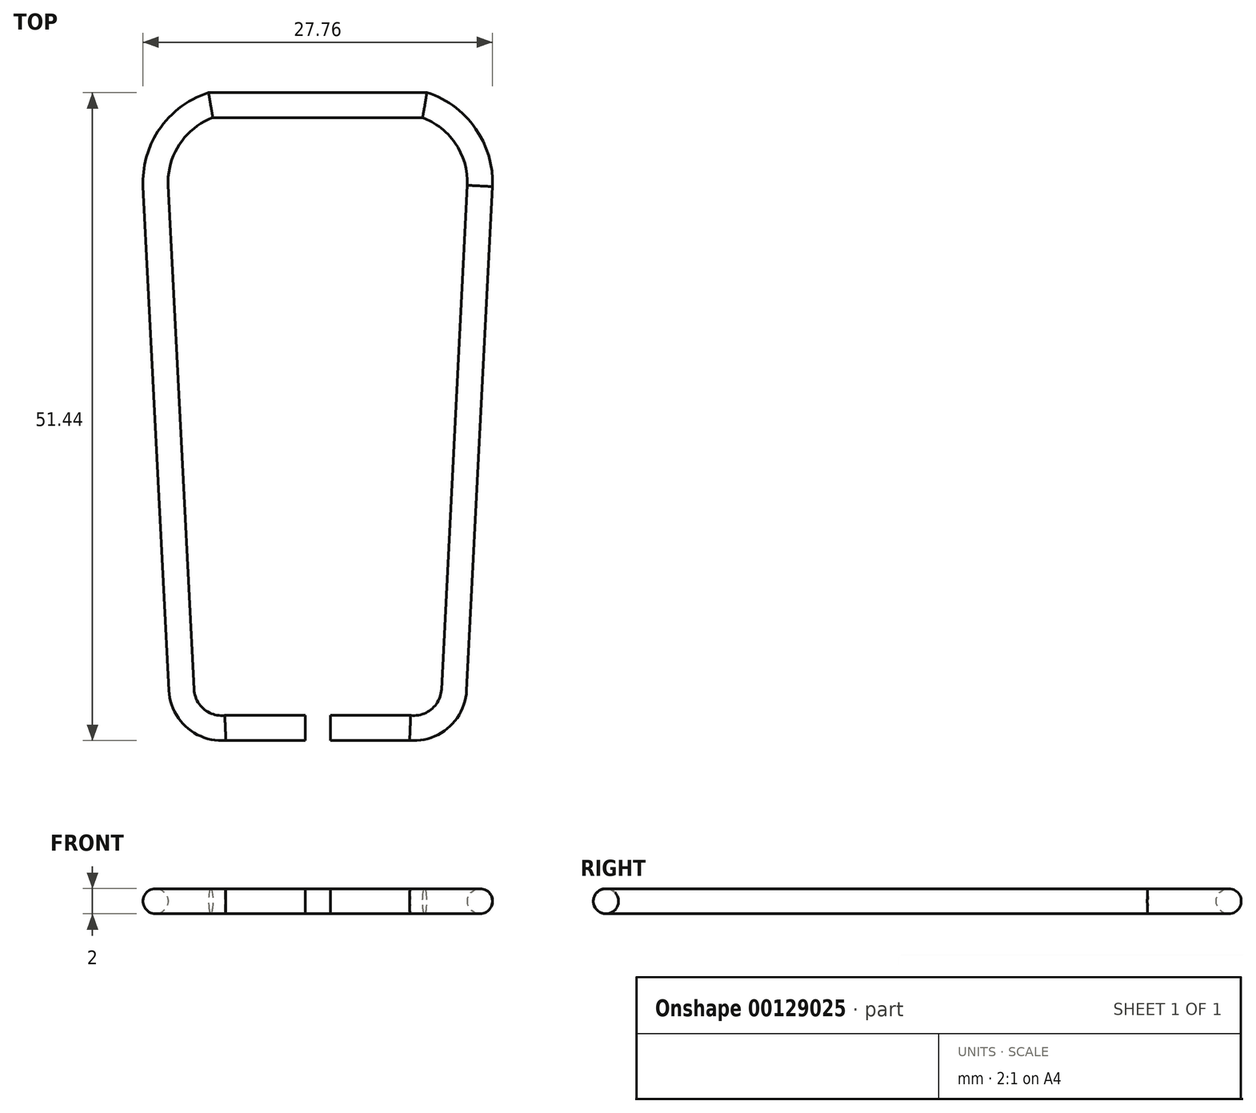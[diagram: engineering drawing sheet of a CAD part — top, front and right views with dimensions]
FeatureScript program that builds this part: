
annotation { "Feature Type Name" : "Feature", "Feature Type Description" : "" }
export const myFeature = defineFeature(function(context is Context, id is Id, definition is map)
    precondition{}
    {
        {
            var Q0;
            Q0=qCreatedBy(makeId("Top.planeOp"),FACE);
            var sketch = newSketch(context, id + "F0", { "sketchPlane" : qUnion([Q0])});
            skArc(sketch, "E0.0", {"start": v(-8.5, 33.52) * mm, "mid": v(-11.75, 31.03) * mm, "end": v(-12.88, 27.1) * mm});
            skLineSegment(sketch, "E0.2", {"start": v(-12.88, 27.1) * mm, "end": v(-10.82, -12.9) * mm});
            skArc(sketch, "E0.4", {"start": v(-10.82, -12.9) * mm, "mid": v(-9.72, -15.15) * mm, "end": v(-7.34, -15.92) * mm});
            skPoint(sketch, "E1.end.orphan", {"position": v(-15, 25.17) * mm});
            skLineSegment(sketch, "E2", {"start": v(-7.34, -15.92) * mm, "end": v(-1, -15.92) * mm});
            skPoint(sketch, "E3", {"position": v(-11.48, 0) * mm});
            skArc(sketch, "E4.MirrorCS", {"start": v(8.5, 33.52) * mm, "mid": v(11.75, 31.03) * mm, "end": v(12.88, 27.1) * mm});
            skLineSegment(sketch, "E5.MirrorCS", {"start": v(12.88, 27.1) * mm, "end": v(10.82, -12.9) * mm});
            skArc(sketch, "E6.MirrorCS", {"start": v(10.82, -12.9) * mm, "mid": v(9.72, -15.15) * mm, "end": v(7.34, -15.92) * mm});
            skLineSegment(sketch, "E7.MirrorCS", {"start": v(7.34, -15.92) * mm, "end": v(1, -15.92) * mm});
            skLineSegment(sketch, "E8", {"start": v(-8.5, 33.52) * mm, "end": v(8.5, 33.52) * mm});
            skSolve(sketch);
        }
        {
            var Q0;
            Q0=qCreatedBy(makeId("Right.planeOp"),FACE);
            cPlane(context, id + "F1", {"entities" : qUnion([Q0]), "cplaneType" : CPlaneType.OFFSET, "offset" : 1 * mm, "width" : 150 * mm, "height" : 150 * mm});
        }
        {
            var Q0;
            Q0=qCreatedBy(id+"F1.planeOp",FACE);
            var sketch = newSketch(context, id + "F2", { "sketchPlane" : qUnion([Q0])});
            skPoint(sketch, "E9.0", {"position": v(-15.92, 0) * mm});
            skCircle(sketch, "E10", {"center": v(-15.92, 0) * mm, "radius": 1 * mm});
            skSolve(sketch);
        }
        {
            var Q0;
            Q0 = qSketchRegion(id + "F2", true);
            var Q1;
            Q1=sQuery(id+"F0.wireOp",EDGE,"E7.MirrorCS");
            var Q2;
            Q2=sQuery(id+"F0.wireOp",EDGE,"E6.MirrorCS");
            var Q3;
            Q3=sQuery(id+"F0.wireOp",EDGE,"E5.MirrorCS");
            var Q4;
            Q4=sQuery(id+"F0.wireOp",EDGE,"E4.MirrorCS");
            var Q5;
            Q5=sQuery(id+"F0.wireOp",EDGE,"E8");
            var Q6;
            Q6=sQuery(id+"F0.wireOp",EDGE,"E0.0");
            var Q7;
            Q7=sQuery(id+"F0.wireOp",EDGE,"E0.2");
            var Q8;
            Q8=sQuery(id+"F0.wireOp",EDGE,"E0.4");
            var Q9;
            Q9=sQuery(id+"F0.wireOp",EDGE,"E2");
            sweep(context, id + "F3", {"profiles" : qUnion([Q0]), "path" : qUnion([Q1, Q2, Q3, Q4, Q5, Q6, Q7, Q8, Q9])});
        }
    });
